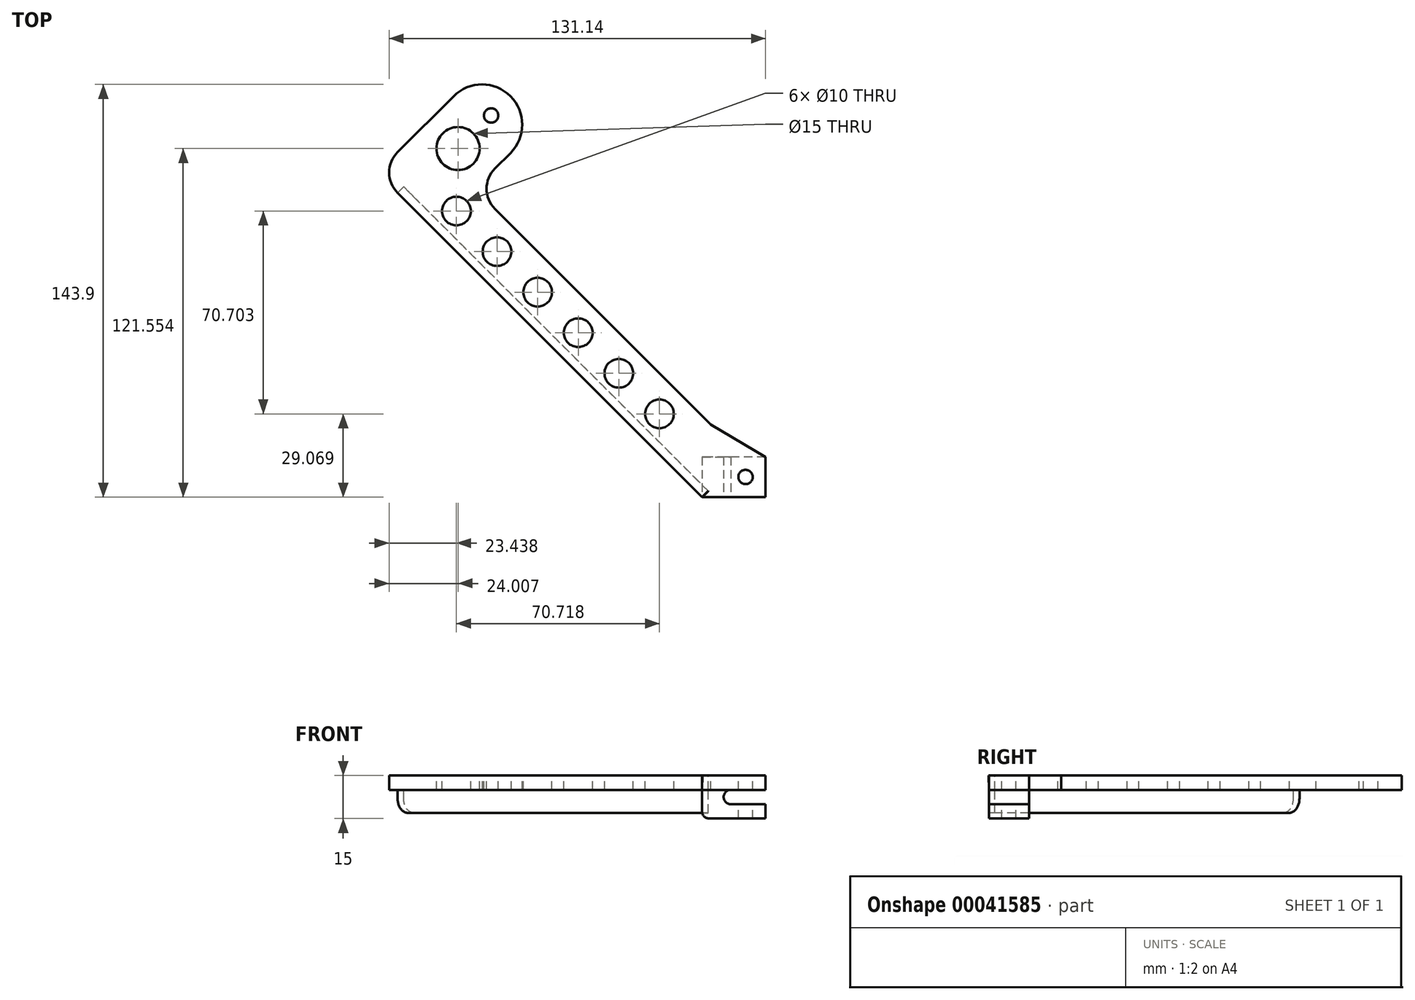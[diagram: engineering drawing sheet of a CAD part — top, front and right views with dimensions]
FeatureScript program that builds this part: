
annotation { "Feature Type Name" : "Feature", "Feature Type Description" : "" }
export const myFeature = defineFeature(function(context is Context, id is Id, definition is map)
    precondition{}
    {
        {
            var Q0;
            Q0=qCreatedBy(makeId("Top.planeOp"),FACE);
            var sketch = newSketch(context, id + "F0", { "sketchPlane" : qUnion([Q0])});
            skLineSegment(sketch, "E0", {"start": v(0, 0) * mm, "end": v(15, 0) * mm, "construction": true});
            skLineSegment(sketch, "E1", {"start": v(0, 0) * mm, "end": v(-113.2, 113.2) * mm, "construction": true});
            skLineSegment(sketch, "E2", {"start": v(0, 0) * mm, "end": v(0, 74.83) * mm, "construction": true});
            skLineSegment(sketch, "E3.0", {"start": v(-4.08, 18.23) * mm, "end": v(-79.27, 93.4) * mm});
            skLineSegment(sketch, "E4.0", {"start": v(-7.14, -7) * mm, "end": v(-113.2, 99.07) * mm});
            skLineSegment(sketch, "E5.0", {"start": v(-7.14, -7) * mm, "end": v(15, -7) * mm});
            skLineSegment(sketch, "E6", {"start": v(15, 7) * mm, "end": v(15, -7) * mm});
            skLineSegment(sketch, "E7", {"start": v(-79.27, 107.55) * mm, "end": v(-73.89, 112.93) * mm});
            skLineSegment(sketch, "E8.0", {"start": v(-113.2, 113.2) * mm, "end": v(-93.69, 132.73) * mm});
            skArc(sketch, "E9", {"start": v(-73.89, 112.93) * mm, "mid": v(-73.89, 132.73) * mm, "end": v(-93.69, 132.73) * mm});
            skLineSegment(sketch, "E10", {"start": v(-73.89, 132.73) * mm, "end": v(-110.38, 96.24) * mm, "construction": true});
            skCircle(sketch, "E11", {"center": v(-80.6, 126.01) * mm, "radius": 2.5 * mm});
            skLineSegment(sketch, "E12", {"start": v(-4.08, 18.23) * mm, "end": v(15, 7) * mm});
            skPoint(sketch, "E13.visualSharp", {"position": v(-86.34, 100.48) * mm});
            skArc(sketch, "E13.filletArc", {"start": v(-79.27, 107.55) * mm, "mid": v(-82.2, 100.48) * mm, "end": v(-79.27, 93.4) * mm});
            skPoint(sketch, "E14.visualSharp", {"position": v(-120.28, 106.14) * mm});
            skArc(sketch, "E14.filletArc", {"start": v(-113.2, 113.2) * mm, "mid": v(-116.14, 106.14) * mm, "end": v(-113.2, 99.07) * mm});
            skCircle(sketch, "E15", {"center": v(-92.13, 114.48) * mm, "radius": 7.5 * mm});
            skCircle(sketch, "E16", {"center": v(-92.7, 92.7) * mm, "radius": 5 * mm});
            skCircle(sketch, "E17.1.0.0", {"center": v(-78.56, 78.56) * mm, "radius": 5 * mm});
            skCircle(sketch, "E17.2.0.0", {"center": v(-64.41, 64.42) * mm, "radius": 5 * mm});
            skCircle(sketch, "E17.3.0.0", {"center": v(-50.27, 50.28) * mm, "radius": 5 * mm});
            skCircle(sketch, "E17.4.0.0", {"center": v(-36.13, 36.14) * mm, "radius": 5 * mm});
            skCircle(sketch, "E17.5.0.0", {"center": v(-21.98, 22) * mm, "radius": 5 * mm});
            skLineSegment(sketch, "E17.direction1", {"start": v(-92.7, 92.7) * mm, "end": v(-78.56, 78.56) * mm, "construction": true});
            skSolve(sketch);
        }
        {
            var Q0;
            Q0=makeQuery(id+"F0.imprint","IMPRINT",FACE,{"disambiguationData":[TD([[makeQuery(id+"F0.imprint","IMPRINT",EDGE,{"derivedFrom":sQuery(id+"F0.wireOp",EDGE,"E3.0")}),1.0]])]});
            extrude(context, id + "F1", {"entities" : qUnion([Q0]), "depth" : 5 * mm});
        }
        {
            var Q0;
            Q0=makeQuery(id+"F1.opExtrude","SWEPT_FACE",FACE,{"disambiguationData":[OSD([sQuery(id+"F0.wireOp",EDGE,"E5.0")])]});
            var sketch = newSketch(context, id + "F2", { "sketchPlane" : qUnion([Q0])});
            skLineSegment(sketch, "E18.bottom", {"start": v(15, 0) * mm, "end": v(-7.14, 0) * mm});
            skLineSegment(sketch, "E18.top", {"start": v(15, 5) * mm, "end": v(2.86, 5) * mm});
            skLineSegment(sketch, "E18.left", {"start": v(15, 0) * mm, "end": v(15, 5) * mm});
            skLineSegment(sketch, "E18.right", {"start": v(-7.14, 0) * mm, "end": v(-7.14, 5) * mm});
            skLineSegment(sketch, "E19", {"start": v(15, 0) * mm, "end": v(15, 15) * mm});
            skLineSegment(sketch, "E20", {"start": v(15, 15) * mm, "end": v(-4.64, 15) * mm});
            skLineSegment(sketch, "E21", {"start": v(-7.14, 12.5) * mm, "end": v(-7.14, 5) * mm});
            skLineSegment(sketch, "E22.0", {"start": v(15, 10) * mm, "end": v(2.86, 10) * mm});
            skLineSegment(sketch, "E23.0", {"start": v(20, 5) * mm, "end": v(-7.14, 5) * mm});
            skLineSegment(sketch, "E24.0", {"start": v(0.36, 7.5) * mm, "end": v(0.36, 7.5) * mm});
            skArc(sketch, "E25.filletArc", {"start": v(2.86, 10) * mm, "mid": v(1.1, 9.27) * mm, "end": v(0.36, 7.5) * mm});
            skArc(sketch, "E26.filletArc", {"start": v(0.36, 7.5) * mm, "mid": v(1.1, 5.73) * mm, "end": v(2.86, 5) * mm});
            skLineSegment(sketch, "E27", {"start": v(15, 10) * mm, "end": v(15, 5) * mm});
            skPoint(sketch, "E28.visualSharp", {"position": v(-7.14, 15) * mm});
            skArc(sketch, "E28.filletArc", {"start": v(-4.64, 15) * mm, "mid": v(-6.4, 14.27) * mm, "end": v(-7.14, 12.5) * mm});
            skPoint(sketch, "E29.newPointB", {"position": v(-7.14, 5) * mm});
            skSolve(sketch);
        }
        {
            var Q0;
            {var subQ5=sQuery(id+"F2.wireOp",EDGE,"E20");Q0=makeQuery(id+"F2.imprint","IMPRINT",FACE,{"disambiguationData":[TD([[makeQuery(id+"F2.imprint","IMPRINT",EDGE,{"derivedFrom":subQ5}),1.0]])]});}
            extrude(context, id + "F3", {"entities" : qUnion([Q0]), "oppositeDirection" : true, "depth" : 14 * mm});
        }
        {
            var Q0;
            Q0=makeQuery(id+"F1.opExtrude","SWEPT_FACE",FACE,{"disambiguationData":[OSD([sQuery(id+"F0.wireOp",EDGE,"E4.0")])]});
            var sketch = newSketch(context, id + "F4", { "sketchPlane" : qUnion([Q0])});
            skLineSegment(sketch, "E30", {"start": v(-0.1, 5) * mm, "end": v(-150.1, 5) * mm});
            skPoint(sketch, "E31.endSnap0", {"position": v(-75.1, 5) * mm});
            skLineSegment(sketch, "E32", {"start": v(-150.1, 8) * mm, "end": v(-150.1, 5) * mm});
            skPoint(sketch, "E33.visualSharp", {"position": v(-150.1, 12.5) * mm});
            skLineSegment(sketch, "E34.0", {"start": v(-0.1, 13) * mm, "end": v(-0.1, 5.08) * mm});
            skArc(sketch, "E35.filletArc", {"start": v(-145.1, 13) * mm, "mid": v(-148.64, 11.53) * mm, "end": v(-150.1, 8) * mm});
            skLineSegment(sketch, "E36", {"start": v(-145.1, 13) * mm, "end": v(-0.1, 13) * mm});
            skLineSegment(sketch, "E37", {"start": v(-0.1, 5.08) * mm, "end": v(0, 0) * mm});
            skLineSegment(sketch, "E38", {"start": v(0, 0) * mm, "end": v(-150.1, 0) * mm});
            skLineSegment(sketch, "E39", {"start": v(-150.1, 0) * mm, "end": v(-150.1, 5) * mm});
            skSolve(sketch);
        }
        {
            var Q0;
            {var subQ4=sQuery(id+"F4.wireOp",EDGE,"E32");Q0=makeQuery(id+"F4.imprint","IMPRINT",FACE,{"disambiguationData":[TD([[makeQuery(id+"F4.imprint","IMPRINT",EDGE,{"derivedFrom":subQ4}),1.0]])]});}
            extrude(context, id + "F5", {"entities" : qUnion([Q0]), "oppositeDirection" : true, "depth" : 3 * mm});
        }
        {
            var Q0;
            Q0=makeQuery(id+"F1.opExtrude","CAP_FACE",FACE,{"disambiguationData":[OSD([sQuery(id+"F0.wireOp",EDGE,"E3.0"),sQuery(id+"F0.wireOp",EDGE,"E4.0"),sQuery(id+"F0.wireOp",EDGE,"E5.0"),sQuery(id+"F0.wireOp",EDGE,"E6"),sQuery(id+"F0.wireOp",EDGE,"E7"),sQuery(id+"F0.wireOp",EDGE,"E8.0"),sQuery(id+"F0.wireOp",EDGE,"E9"),sQuery(id+"F0.wireOp",EDGE,"E11"),sQuery(id+"F0.wireOp",EDGE,"E12"),sQuery(id+"F0.wireOp",EDGE,"E13.filletArc"),sQuery(id+"F0.wireOp",EDGE,"E14.filletArc"),sQuery(id+"F0.wireOp",EDGE,"E15"),sQuery(id+"F0.wireOp",EDGE,"E16"),sQuery(id+"F0.wireOp",EDGE,"E17.1.0.0"),sQuery(id+"F0.wireOp",EDGE,"E17.2.0.0"),sQuery(id+"F0.wireOp",EDGE,"E17.3.0.0"),sQuery(id+"F0.wireOp",EDGE,"E17.4.0.0"),sQuery(id+"F0.wireOp",EDGE,"E17.5.0.0")])],"isStart":true});
            var sketch = newSketch(context, id + "F6", { "sketchPlane" : qUnion([Q0])});
            skLineSegment(sketch, "E40", {"start": v(15, 0) * mm, "end": v(-14.14, 0) * mm, "construction": true});
            skLineSegment(sketch, "E41", {"start": v(8, -11.12) * mm, "end": v(8, 7) * mm, "construction": true});
            skCircle(sketch, "E42", {"center": v(8, 0) * mm, "radius": 2.5 * mm});
            skSolve(sketch);
        }
        {
            var Q0;
            Q0=makeQuery(id+"F6.imprint","IMPRINT",FACE,{"disambiguationData":[TD([[makeQuery(id+"F6.imprint","IMPRINT",EDGE,{"derivedFrom":sQuery(id+"F6.wireOp",EDGE,"E42")}),1.0]])]});
            extrude(context, id + "F7", {"entities" : qUnion([Q0]), "operationType" : NewBodyOperationType.REMOVE, "oppositeDirection" : true, "depth" : 25 * mm});
        }
        {
            var Q0;
            Q0=makeQuery(id+"F3.opExtrude","SWEPT_FACE",FACE,{"disambiguationData":[OSD([sQuery(id+"F2.wireOp",EDGE,"E20")])]});
            var sketch = newSketch(context, id + "F8", { "sketchPlane" : qUnion([Q0])});
            skLineSegment(sketch, "E43", {"start": v(15, 0) * mm, "end": v(-4.64, 0) * mm, "construction": true});
            skLineSegment(sketch, "E44", {"start": v(8, -7) * mm, "end": v(8, 7) * mm, "construction": true});
            skCircle(sketch, "E45", {"center": v(8, 0) * mm, "radius": 2.5 * mm});
            skSolve(sketch);
        }
        {
            var Q0;
            Q0=makeQuery(id+"F8.imprint","IMPRINT",FACE,{"disambiguationData":[TD([[makeQuery(id+"F8.imprint","IMPRINT",EDGE,{"derivedFrom":sQuery(id+"F8.wireOp",EDGE,"E45")}),1.0]])]});
            extrude(context, id + "F9", {"entities" : qUnion([Q0]), "operationType" : NewBodyOperationType.REMOVE, "oppositeDirection" : true, "depth" : 5 * mm});
        }
        {
            var Q0;
            Q0=makeQuery(id+"F1.opExtrude","SWEPT_BODY",BODY,{"disambiguationData":[OSD([sQuery(id+"F0.wireOp",EDGE,"E3.0"),sQuery(id+"F0.wireOp",EDGE,"E4.0"),sQuery(id+"F0.wireOp",EDGE,"E5.0"),sQuery(id+"F0.wireOp",EDGE,"E6"),sQuery(id+"F0.wireOp",EDGE,"E7"),sQuery(id+"F0.wireOp",EDGE,"E8.0"),sQuery(id+"F0.wireOp",EDGE,"E9"),sQuery(id+"F0.wireOp",EDGE,"E11"),sQuery(id+"F0.wireOp",EDGE,"E12"),sQuery(id+"F0.wireOp",EDGE,"E13.filletArc"),sQuery(id+"F0.wireOp",EDGE,"E14.filletArc"),sQuery(id+"F0.wireOp",EDGE,"E15"),sQuery(id+"F0.wireOp",EDGE,"E16"),sQuery(id+"F0.wireOp",EDGE,"E17.1.0.0"),sQuery(id+"F0.wireOp",EDGE,"E17.2.0.0"),sQuery(id+"F0.wireOp",EDGE,"E17.3.0.0"),sQuery(id+"F0.wireOp",EDGE,"E17.4.0.0"),sQuery(id+"F0.wireOp",EDGE,"E17.5.0.0")])]});
            var Q1;
            Q1=makeQuery(id+"F3.opExtrude","SWEPT_BODY",BODY,{"disambiguationData":[OSD([sQuery(id+"F2.wireOp",EDGE,"E19"),sQuery(id+"F2.wireOp",EDGE,"E20"),sQuery(id+"F2.wireOp",EDGE,"E21"),sQuery(id+"F2.wireOp",EDGE,"E22.0"),sQuery(id+"F2.wireOp",EDGE,"E23.0"),sQuery(id+"F2.wireOp",EDGE,"E25.filletArc"),sQuery(id+"F2.wireOp",EDGE,"E26.filletArc"),sQuery(id+"F2.wireOp",EDGE,"E28.filletArc")])]});
            var Q2;
            Q2=makeQuery(id+"F5.opExtrude","SWEPT_BODY",BODY,{"disambiguationData":[OSD([sQuery(id+"F4.wireOp",EDGE,"E32"),sQuery(id+"F4.wireOp",EDGE,"E34.0"),sQuery(id+"F4.wireOp",EDGE,"E35.filletArc"),sQuery(id+"F4.wireOp",EDGE,"0cdfd59c-7c3e-4337-9c50-35a9dc602817"),sQuery(id+"F4.wireOp",EDGE,"E36")])]});
            var Q3;
            Q3=makeQuery(id+"F1.opExtrude","CAP_FACE",FACE,{"disambiguationData":[OSD([sQuery(id+"F0.wireOp",EDGE,"E3.0"),sQuery(id+"F0.wireOp",EDGE,"E4.0"),sQuery(id+"F0.wireOp",EDGE,"E5.0"),sQuery(id+"F0.wireOp",EDGE,"E6"),sQuery(id+"F0.wireOp",EDGE,"E7"),sQuery(id+"F0.wireOp",EDGE,"E8.0"),sQuery(id+"F0.wireOp",EDGE,"E9"),sQuery(id+"F0.wireOp",EDGE,"E11"),sQuery(id+"F0.wireOp",EDGE,"E12"),sQuery(id+"F0.wireOp",EDGE,"E13.filletArc"),sQuery(id+"F0.wireOp",EDGE,"E14.filletArc"),sQuery(id+"F0.wireOp",EDGE,"E15"),sQuery(id+"F0.wireOp",EDGE,"E16"),sQuery(id+"F0.wireOp",EDGE,"E17.1.0.0"),sQuery(id+"F0.wireOp",EDGE,"E17.2.0.0"),sQuery(id+"F0.wireOp",EDGE,"E17.3.0.0"),sQuery(id+"F0.wireOp",EDGE,"E17.4.0.0"),sQuery(id+"F0.wireOp",EDGE,"E17.5.0.0")])],"isStart":true});
            mirror(context, id + "F10", {"entities" : qUnion([Q0, Q1, Q2]), "mirrorPlane" : qUnion([Q3])});
        }
        {
            var Q0;
            Q0=makeQuery(id+"F1.opExtrude","SWEPT_BODY",BODY,{"disambiguationData":[OSD([sQuery(id+"F0.wireOp",EDGE,"E3.0"),sQuery(id+"F0.wireOp",EDGE,"E4.0"),sQuery(id+"F0.wireOp",EDGE,"E5.0"),sQuery(id+"F0.wireOp",EDGE,"E6"),sQuery(id+"F0.wireOp",EDGE,"E7"),sQuery(id+"F0.wireOp",EDGE,"E8.0"),sQuery(id+"F0.wireOp",EDGE,"E9"),sQuery(id+"F0.wireOp",EDGE,"E11"),sQuery(id+"F0.wireOp",EDGE,"E12"),sQuery(id+"F0.wireOp",EDGE,"E13.filletArc"),sQuery(id+"F0.wireOp",EDGE,"E14.filletArc"),sQuery(id+"F0.wireOp",EDGE,"E15"),sQuery(id+"F0.wireOp",EDGE,"E16"),sQuery(id+"F0.wireOp",EDGE,"E17.1.0.0"),sQuery(id+"F0.wireOp",EDGE,"E17.2.0.0"),sQuery(id+"F0.wireOp",EDGE,"E17.3.0.0"),sQuery(id+"F0.wireOp",EDGE,"E17.4.0.0"),sQuery(id+"F0.wireOp",EDGE,"E17.5.0.0")])]});
            deleteBodies(context, id + "F11", {"entities" : qUnion([Q0])});
        }
        {
            var Q0;
            Q0=makeQuery(id+"F5.opExtrude","SWEPT_BODY",BODY,{"disambiguationData":[OSD([sQuery(id+"F4.wireOp",EDGE,"E32"),sQuery(id+"F4.wireOp",EDGE,"E34.0"),sQuery(id+"F4.wireOp",EDGE,"E35.filletArc"),sQuery(id+"F4.wireOp",EDGE,"0cdfd59c-7c3e-4337-9c50-35a9dc602817"),sQuery(id+"F4.wireOp",EDGE,"E36")])]});
            deleteBodies(context, id + "F12", {"entities" : qUnion([Q0])});
        }
        {
            var Q0;
            Q0=makeQuery(id+"F3.opExtrude","SWEPT_BODY",BODY,{"disambiguationData":[OSD([sQuery(id+"F2.wireOp",EDGE,"E19"),sQuery(id+"F2.wireOp",EDGE,"E20"),sQuery(id+"F2.wireOp",EDGE,"E21"),sQuery(id+"F2.wireOp",EDGE,"E22.0"),sQuery(id+"F2.wireOp",EDGE,"E23.0"),sQuery(id+"F2.wireOp",EDGE,"E25.filletArc"),sQuery(id+"F2.wireOp",EDGE,"E26.filletArc"),sQuery(id+"F2.wireOp",EDGE,"E28.filletArc")])]});
            deleteBodies(context, id + "F13", {"entities" : qUnion([Q0])});
        }
    });
